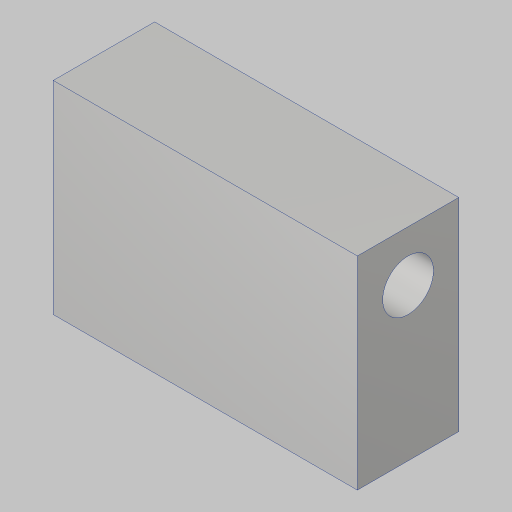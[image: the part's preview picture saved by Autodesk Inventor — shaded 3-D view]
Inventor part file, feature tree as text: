
AUTODESK INVENTOR PART (.ipt)
format: ipt  version: 2023.5 (Build 275446000, 446)  size: 100,864 bytes
history: native  units: in
note: dims shown in document units (in); Inventor stores cm internally (conversion verified against a paired STEP export)
features: sketch x2, extrude x1, hole x1
ambient origin geometry x8: Origin, YZ Plane, XZ Plane, XY Plane, X Axis, Y Axis, Z Axis, Center Point
bodies: Solid1 (feature_tree)
feature tree (4):
  extrude  "Extrusion1"  Depth=1.0in
  hole  "Hole1"  [1 undecoded]
  sketch  "Sketch1"  dims[d0=2.0in d1=1.0in]
  sketch  "Sketch2"  dims[d2=3.0in d3=0.0in d4=0.5in d5=0.5in d6=0.75in d7=0.385in d8=0.25in d9=0.5635in d10=1.0in d11=0.8108in]
note: 1 required parameter value undecoded (feature->parameter linkage not recoverable at this tier; creation-order binding heuristic only, values carry confidence <= 0.55)
